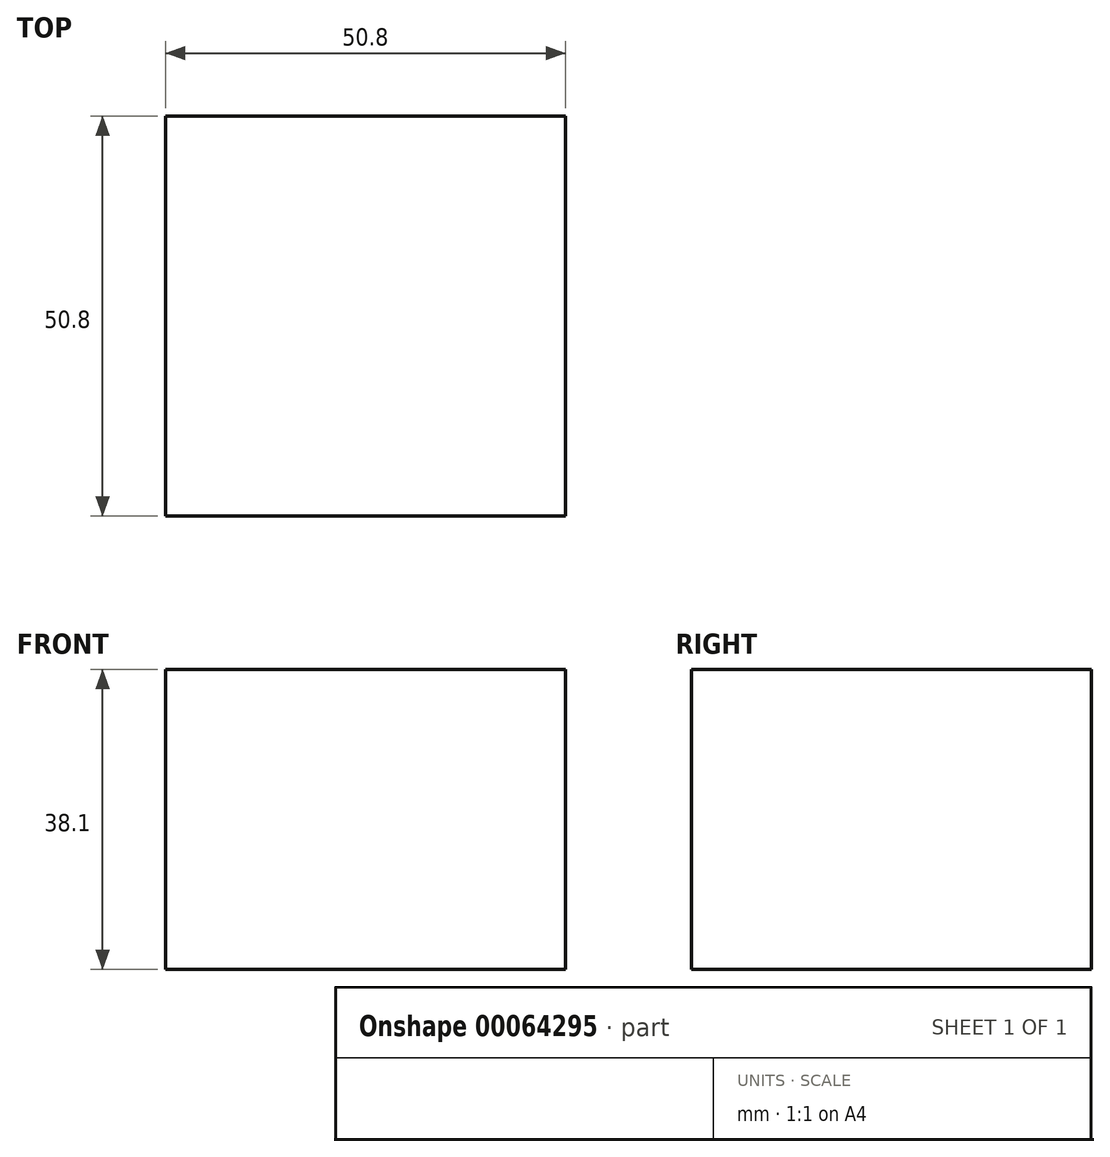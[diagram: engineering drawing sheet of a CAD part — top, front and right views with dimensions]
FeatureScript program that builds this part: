
annotation { "Feature Type Name" : "Feature", "Feature Type Description" : "" }
export const myFeature = defineFeature(function(context is Context, id is Id, definition is map)
    precondition{}
    {
        {
            var Q0;
            Q0=qCreatedBy(makeId("Top.planeOp"),FACE);
            var sketch = newSketch(context, id + "F0", { "sketchPlane" : qUnion([Q0])});
            skLineSegment(sketch, "E0.bottom", {"start": v(-25.4, 25.4) * mm, "end": v(25.4, 25.4) * mm});
            skLineSegment(sketch, "E0.top", {"start": v(-25.4, -25.4) * mm, "end": v(25.4, -25.4) * mm});
            skLineSegment(sketch, "E0.left", {"start": v(-25.4, 25.4) * mm, "end": v(-25.4, -25.4) * mm});
            skLineSegment(sketch, "E0.right", {"start": v(25.4, 25.4) * mm, "end": v(25.4, -25.4) * mm});
            skCircle(sketch, "E1", {"center": v(0, 0) * mm, "radius": 12.7 * mm});
            skSolve(sketch);
        }
        {
            var Q0;
            Q0 = qSketchRegion(id + "F0", true);
            var Q1;
            Q1=makeQuery(id+"F0.imprint","IMPRINT",FACE,{"disambiguationData":[TD([[makeQuery(id+"F0.imprint","IMPRINT",EDGE,{"derivedFrom":sQuery(id+"F0.wireOp",EDGE,"E1")}),1.0]])]});
            extrude(context, id + "F1", {"entities" : qUnion([Q0, Q1]), "depth" : 25.4 * mm, "hasSecondDirection" : true, "secondDirectionOppositeDirection" : true, "secondDirectionDepth" : 12.7 * mm});
        }
    });
